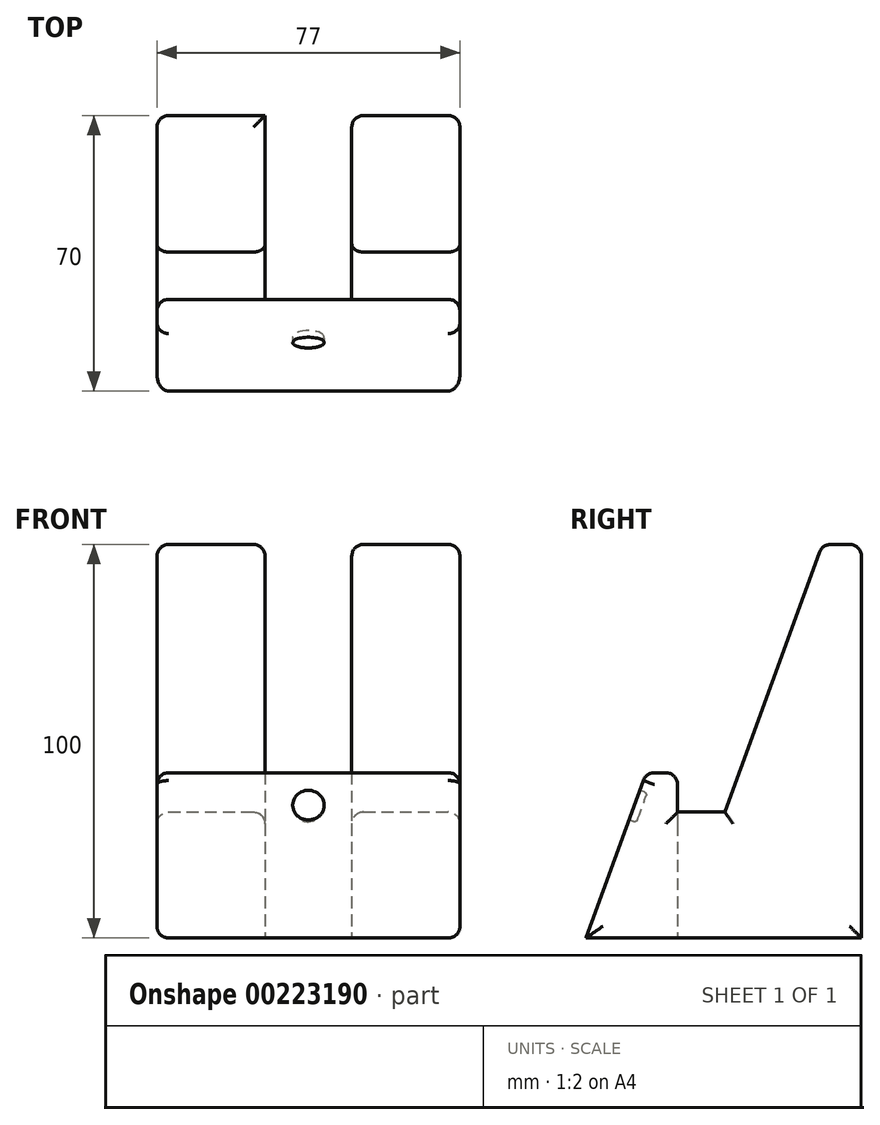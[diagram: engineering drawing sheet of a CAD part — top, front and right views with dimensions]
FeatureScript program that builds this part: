
annotation { "Feature Type Name" : "Feature", "Feature Type Description" : "" }
export const myFeature = defineFeature(function(context is Context, id is Id, definition is map)
    precondition{}
    {
        {
            var Q0;
            Q0=qCreatedBy(makeId("Right.planeOp"),FACE);
            var sketch = newSketch(context, id + "F0", { "sketchPlane" : qUnion([Q0])});
            skLineSegment(sketch, "E0", {"start": v(0, 0) * mm, "end": v(-70, 0) * mm});
            skLineSegment(sketch, "E1", {"start": v(-70, 0) * mm, "end": v(-54.71, 42) * mm});
            skLineSegment(sketch, "E2", {"start": v(-54.71, 42) * mm, "end": v(-46.71, 42) * mm});
            skLineSegment(sketch, "E3", {"start": v(-46.71, 42) * mm, "end": v(-46.71, 32) * mm});
            skLineSegment(sketch, "E4", {"start": v(-46.71, 32) * mm, "end": v(-34.71, 32) * mm});
            skLineSegment(sketch, "E5", {"start": v(-34.71, 32) * mm, "end": v(-9.96, 100) * mm});
            skLineSegment(sketch, "E6", {"start": v(-9.96, 100) * mm, "end": v(0, 100) * mm});
            skLineSegment(sketch, "E7", {"start": v(0, 100) * mm, "end": v(0, 0) * mm});
            skSolve(sketch);
        }
        {
            var Q0;
            Q0=makeQuery(id+"F0.imprint","IMPRINT",FACE,{"disambiguationData":[TD([[makeQuery(id+"F0.imprint","IMPRINT",EDGE,{"derivedFrom":sQuery(id+"F0.wireOp",EDGE,"E0")}),-1.0]])]});
            extrude(context, id + "F1", {"entities" : qUnion([Q0]), "endBound" : BoundingType.SYMMETRIC, "oppositeDirection" : true, "depth" : 77 * mm});
        }
        {
            var Q0;
            Q0=makeQuery(id+"F1.opExtrude","SWEPT_FACE",FACE,{"disambiguationData":[OSD([sQuery(id+"F0.wireOp",EDGE,"E7")])]});
            var sketch = newSketch(context, id + "F2", { "sketchPlane" : qUnion([Q0])});
            skLineSegment(sketch, "E8.bottom", {"start": v(-11, 100) * mm, "end": v(11, 100) * mm});
            skLineSegment(sketch, "E8.top", {"start": v(-11, 0) * mm, "end": v(11, 0) * mm});
            skLineSegment(sketch, "E8.left", {"start": v(-11, 100) * mm, "end": v(-11, 0) * mm});
            skLineSegment(sketch, "E8.right", {"start": v(11, 100) * mm, "end": v(11, 0) * mm});
            skPoint(sketch, "E8.middle", {"position": v(0, 50) * mm});
            skSolve(sketch);
        }
        {
            var Q0;
            Q0 = qSketchRegion(id + "F2", true);
            var Q1;
            Q1=makeQuery(id+"F1.opExtrude","SWEPT_FACE",FACE,{"disambiguationData":[OSD([sQuery(id+"F0.wireOp",EDGE,"E3")])]});
            extrude(context, id + "F3", {"entities" : qUnion([Q0]), "operationType" : NewBodyOperationType.REMOVE, "endBound" : BoundingType.UP_TO_SURFACE, "oppositeDirection" : true, "endBoundEntityFace" : qUnion([Q1]), "depth" : 46.7 * mm});
        }
        {
            var Q0;
            Q0=makeQuery(id+"F1.opExtrude","SWEPT_FACE",FACE,{"disambiguationData":[OSD([sQuery(id+"F0.wireOp",EDGE,"E1")])]});
            var sketch = newSketch(context, id + "F4", { "sketchPlane" : qUnion([Q0])});
            skCircle(sketch, "E9", {"center": v(0, 12) * mm, "radius": 4 * mm});
            skPoint(sketch, "E10", {"position": v(0, 0) * mm});
            skSolve(sketch);
        }
        {
            var Q0;
            Q0=makeQuery(id+"F4.imprint","IMPRINT",FACE,{"disambiguationData":[TD([[makeQuery(id+"F4.imprint","IMPRINT",EDGE,{"derivedFrom":sQuery(id+"F4.wireOp",EDGE,"E9")}),1.0]])]});
            extrude(context, id + "F5", {"entities" : qUnion([Q0]), "operationType" : NewBodyOperationType.REMOVE, "oppositeDirection" : true, "depth" : 2 * mm});
        }
        {
            var Q0;
            Q0=makeQuery(id+"F5.boolean.opBoolean","COPY",EDGE,{"derivedFrom":makeQuery(id+"F5.opExtrude","CAP_EDGE",EDGE,{"disambiguationData":[OSD([sQuery(id+"F4.wireOp",EDGE,"E9")])],"isStart":false})});
            var Q1;
            Q1=makeQuery(id+"F5.boolean.opBoolean","COPY",EDGE,{"derivedFrom":makeQuery(id+"F5.opExtrude","CAP_EDGE",EDGE,{"disambiguationData":[OSD([sQuery(id+"F4.wireOp",EDGE,"E9")])],"isStart":true})});
            fillet(context, id + "F6", {"entities" : qUnion([Q0, Q1]), "radius" : .75 * mm, "tangentPropagation" : true, "allowEdgeOverflow" : false});
        }
        {
            var Q0;
            Q0=makeQuery(id+"F1.opExtrude","CAP_FACE",FACE,{"disambiguationData":[OSD([sQuery(id+"F0.wireOp",EDGE,"E0"),sQuery(id+"F0.wireOp",EDGE,"E1"),sQuery(id+"F0.wireOp",EDGE,"E2"),sQuery(id+"F0.wireOp",EDGE,"E3"),sQuery(id+"F0.wireOp",EDGE,"E4"),sQuery(id+"F0.wireOp",EDGE,"E5"),sQuery(id+"F0.wireOp",EDGE,"E6"),sQuery(id+"F0.wireOp",EDGE,"E7")])],"isStart":true});
            var Q1;
            Q1=makeQuery(id+"F1.opExtrude","CAP_FACE",FACE,{"disambiguationData":[OSD([sQuery(id+"F0.wireOp",EDGE,"E0"),sQuery(id+"F0.wireOp",EDGE,"E1"),sQuery(id+"F0.wireOp",EDGE,"E2"),sQuery(id+"F0.wireOp",EDGE,"E3"),sQuery(id+"F0.wireOp",EDGE,"E4"),sQuery(id+"F0.wireOp",EDGE,"E5"),sQuery(id+"F0.wireOp",EDGE,"E6"),sQuery(id+"F0.wireOp",EDGE,"E7")])],"isStart":false});
            var Q2;
            Q2=makeQuery(id+"F3.boolean.opBoolean","COPY",EDGE,{"derivedFrom":makeQuery(id+"F3.opExtrude","CAP_EDGE",EDGE,{"disambiguationData":[OSD([sQuery(id+"F2.wireOp",EDGE,"E8.right")])],"isStart":true})});
            var Q3;
            {var subQ1=sQuery(id+"F0.wireOp",EDGE,"E6");Q3=makeQuery(id+"F3.boolean.opBoolean","SPLIT",FACE,{"disambiguationData":[TD([makeQuery(id+"F3.opExtrude","SWEPT_FACE",FACE,{"disambiguationData":[OSD([sQuery(id+"F2.wireOp",EDGE,"E8.right")])]})])],"derivedFrom":makeQuery(id+"F1.opExtrude","SWEPT_FACE",FACE,{"disambiguationData":[OSD([subQ1])]})});}
            var Q4;
            {var subQ1=sQuery(id+"F0.wireOp",EDGE,"E6");Q4=makeQuery(id+"F3.boolean.opBoolean","SPLIT",FACE,{"disambiguationData":[TD([makeQuery(id+"F3.opExtrude","SWEPT_FACE",FACE,{"disambiguationData":[OSD([sQuery(id+"F2.wireOp",EDGE,"E8.left")])]})])],"derivedFrom":makeQuery(id+"F1.opExtrude","SWEPT_FACE",FACE,{"disambiguationData":[OSD([subQ1])]})});}
            var Q5;
            Q5=makeQuery(id+"F3.boolean.opBoolean","COPY",EDGE,{"derivedFrom":makeQuery(id+"F3.opExtrude","CAP_EDGE",EDGE,{"disambiguationData":[OSD([sQuery(id+"F2.wireOp",EDGE,"E8.left")])],"isStart":true})});
            var Q6;
            Q6=makeQuery(id+"F3.boolean.opBoolean","INTERSECT",EDGE,{"derivedFrom":[makeQuery(id+"F1.opExtrude","SWEPT_FACE",FACE,{"disambiguationData":[OSD([sQuery(id+"F0.wireOp",EDGE,"E5")])]}),makeQuery(id+"F3.opExtrude","SWEPT_FACE",FACE,{"disambiguationData":[OSD([sQuery(id+"F2.wireOp",EDGE,"E8.left")])]})]});
            var Q7;
            Q7=makeQuery(id+"F3.boolean.opBoolean","INTERSECT",EDGE,{"derivedFrom":[makeQuery(id+"F1.opExtrude","SWEPT_FACE",FACE,{"disambiguationData":[OSD([sQuery(id+"F0.wireOp",EDGE,"E5")])]}),makeQuery(id+"F3.opExtrude","SWEPT_FACE",FACE,{"disambiguationData":[OSD([sQuery(id+"F2.wireOp",EDGE,"E8.right")])]})]});
            fillet(context, id + "F7", {"entities" : qUnion([Q0, Q1, Q2, Q3, Q4, Q5, Q6, Q7]), "radius" : 3 * mm, "tangentPropagation" : true, "allowEdgeOverflow" : false});
        }
        {
            var Q0;
            Q0=makeQuery(id+"F1.opExtrude","SWEPT_EDGE",EDGE,{"disambiguationData":[OSD([sQuery(id+"F0.wireOp",EDGE,"E1"),sQuery(id+"F0.wireOp",EDGE,"E2")])]});
            var Q1;
            Q1=makeQuery(id+"F1.opExtrude","SWEPT_EDGE",EDGE,{"disambiguationData":[OSD([sQuery(id+"F0.wireOp",EDGE,"E2"),sQuery(id+"F0.wireOp",EDGE,"E3")])]});
            var Q2;
            Q2=makeQuery(id+"F3.boolean.opBoolean","INTERSECT",EDGE,{"derivedFrom":[makeQuery(id+"F1.opExtrude","SWEPT_FACE",FACE,{"disambiguationData":[OSD([sQuery(id+"F0.wireOp",EDGE,"E4")])]}),makeQuery(id+"F3.opExtrude","SWEPT_FACE",FACE,{"disambiguationData":[OSD([sQuery(id+"F2.wireOp",EDGE,"E8.right")])]})]});
            var Q3;
            Q3=makeQuery(id+"F3.boolean.opBoolean","INTERSECT",EDGE,{"derivedFrom":[makeQuery(id+"F1.opExtrude","SWEPT_FACE",FACE,{"disambiguationData":[OSD([sQuery(id+"F0.wireOp",EDGE,"E4")])]}),makeQuery(id+"F3.opExtrude","SWEPT_FACE",FACE,{"disambiguationData":[OSD([sQuery(id+"F2.wireOp",EDGE,"E8.left")])]})]});
            fillet(context, id + "F8", {"entities" : qUnion([Q0, Q1, Q2, Q3]), "radius" : 3 * mm, "tangentPropagation" : true, "allowEdgeOverflow" : false});
        }
    });
